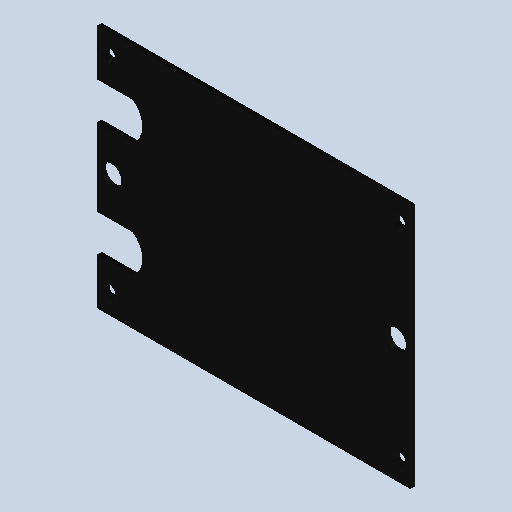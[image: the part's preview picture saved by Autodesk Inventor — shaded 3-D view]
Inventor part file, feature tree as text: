
AUTODESK INVENTOR PART (.ipt)
format: ipt  version: 2022.1 (Build 261234000, 234)  size: 76,800 bytes
history: native  units: mm (DEFAULTED — no unit token found)
features: other x8, chamfer x1
bodies: Body1 (feature_tree)
feature tree (9):
  other  "Sólido1"
  other  "Origen"
  other  "Plano YZ"
  other  "Plano XZ"
  other  "Plano XY"
  other  "Eje X"
  other  "Eje Y"
  other  "Eje Z"
  chamfer  "Chamfer1"  [1 undecoded]
note: 1 required parameter value undecoded (feature->parameter linkage not recoverable at this tier; creation-order binding heuristic only, values carry confidence <= 0.55)
